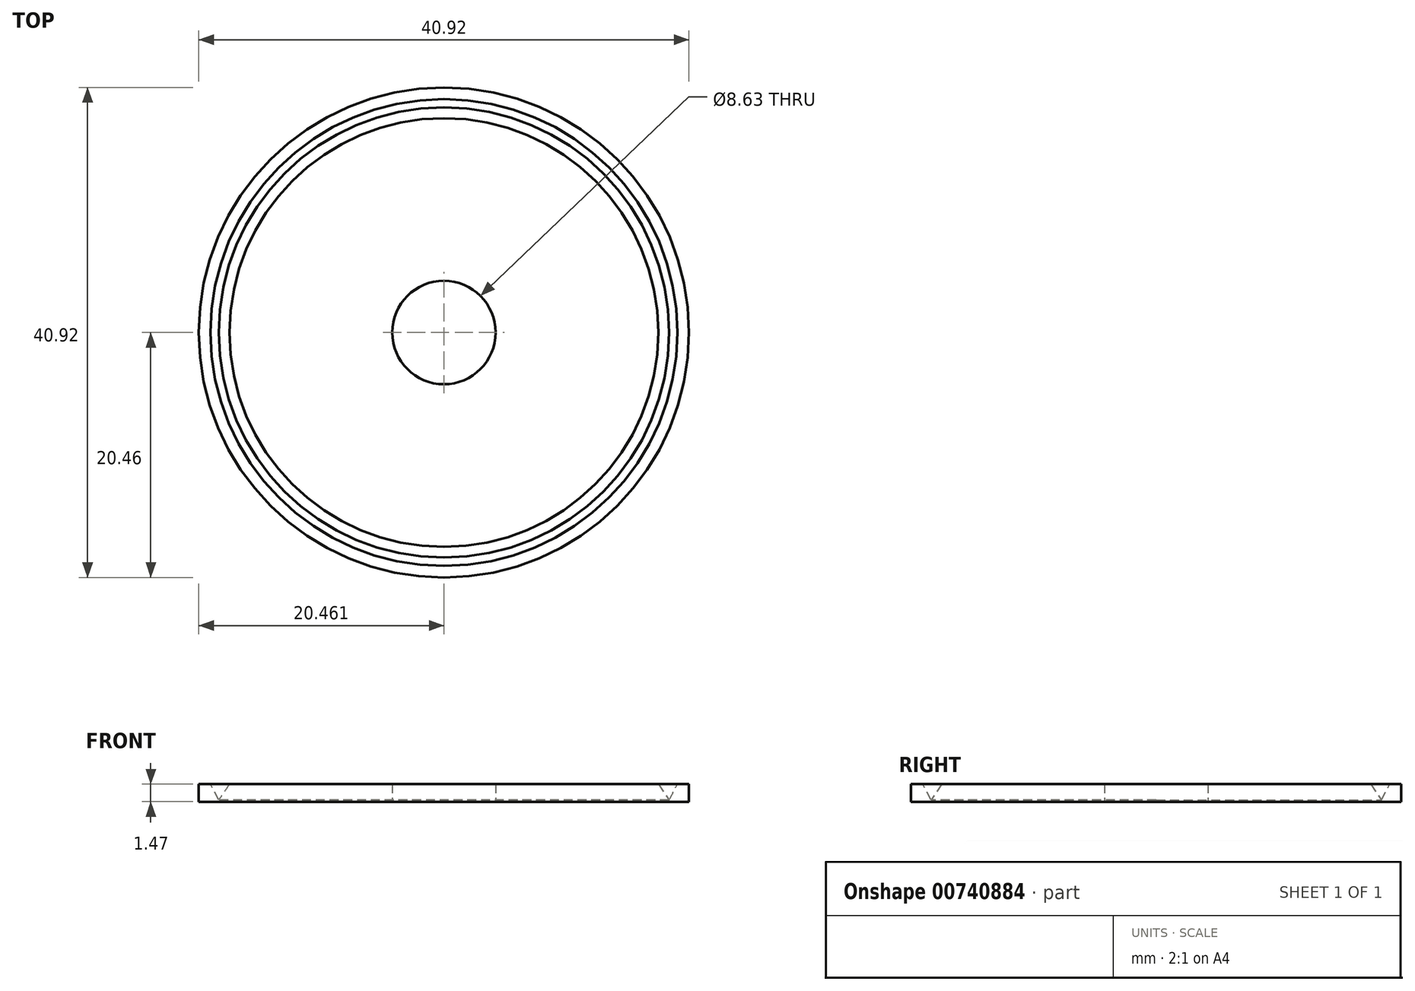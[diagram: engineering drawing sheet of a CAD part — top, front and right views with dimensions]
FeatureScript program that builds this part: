
annotation { "Feature Type Name" : "Feature", "Feature Type Description" : "" }
export const myFeature = defineFeature(function(context is Context, id is Id, definition is map)
    precondition{}
    {
        {
            var Q0;
            Q0=qCreatedBy(makeId("Front.planeOp"),FACE);
            var sketch = newSketch(context, id + "F0", { "sketchPlane" : qUnion([Q0])});
            skLineSegment(sketch, "E0.bottom", {"start": v(-0.44, 15.74) * mm, "end": v(15.7, 15.74) * mm});
            skLineSegment(sketch, "E0.top", {"start": v(-0.44, 14.27) * mm, "end": v(15.7, 14.27) * mm});
            skLineSegment(sketch, "E0.left", {"start": v(-0.44, 15.74) * mm, "end": v(-0.44, 14.27) * mm});
            skLineSegment(sketch, "E0.right", {"start": v(15.7, 15.74) * mm, "end": v(15.7, 14.27) * mm});
            skLineSegment(sketch, "E1", {"start": v(-4.76, -5.16) * mm, "end": v(-4.76, 26.27) * mm, "construction": true});
            skPoint(sketch, "E1.startSnap0", {"position": v(-4.76, 11.2) * mm});
            skLineSegment(sketch, "E2", {"start": v(26.81, 3.24) * mm, "end": v(36.98, 15.91) * mm, "construction": true});
            skLineSegment(sketch, "E3", {"start": v(-27.26, 1.62) * mm, "end": v(-40.37, 16.35) * mm, "construction": true});
            skSolve(sketch);
        }
        {
            var Q0;
            Q0 = qSketchRegion(id + "F0", true);
            var Q1;
            Q1=sQuery(id+"F0.wireOp",EDGE,"E1");
            revolve(context, id + "F1", {"surfaceOperationType" : NewSurfaceOperationType.NEW, "entities" : qUnion([Q0]), "axis" : qUnion([Q1]), "revolveType" : RevolveType.FULL});
        }
        {
            var Q0;
            Q0=qCreatedBy(makeId("Front.planeOp"),FACE);
            var sketch = newSketch(context, id + "F2", { "sketchPlane" : qUnion([Q0])});
            skLineSegment(sketch, "E4", {"start": v(-23.56, 14.4) * mm, "end": v(-22.19, 16.43) * mm});
            skLineSegment(sketch, "E5", {"start": v(-22.19, 16.43) * mm, "end": v(-24.61, 16.43) * mm});
            skLineSegment(sketch, "E6", {"start": v(-24.61, 16.43) * mm, "end": v(-23.56, 14.4) * mm});
            skSolve(sketch);
        }
        {
            var Q0;
            Q0 = qSketchRegion(id + "F2", true);
            var Q1;
            Q1=sQuery(id+"F0.wireOp",EDGE,"E1");
            revolve(context, id + "F3", {"operationType" : NewBodyOperationType.REMOVE, "surfaceOperationType" : NewSurfaceOperationType.NEW, "entities" : qUnion([Q0]), "axis" : qUnion([Q1]), "revolveType" : RevolveType.FULL, "oppositeDirection" : true});
        }
    });
